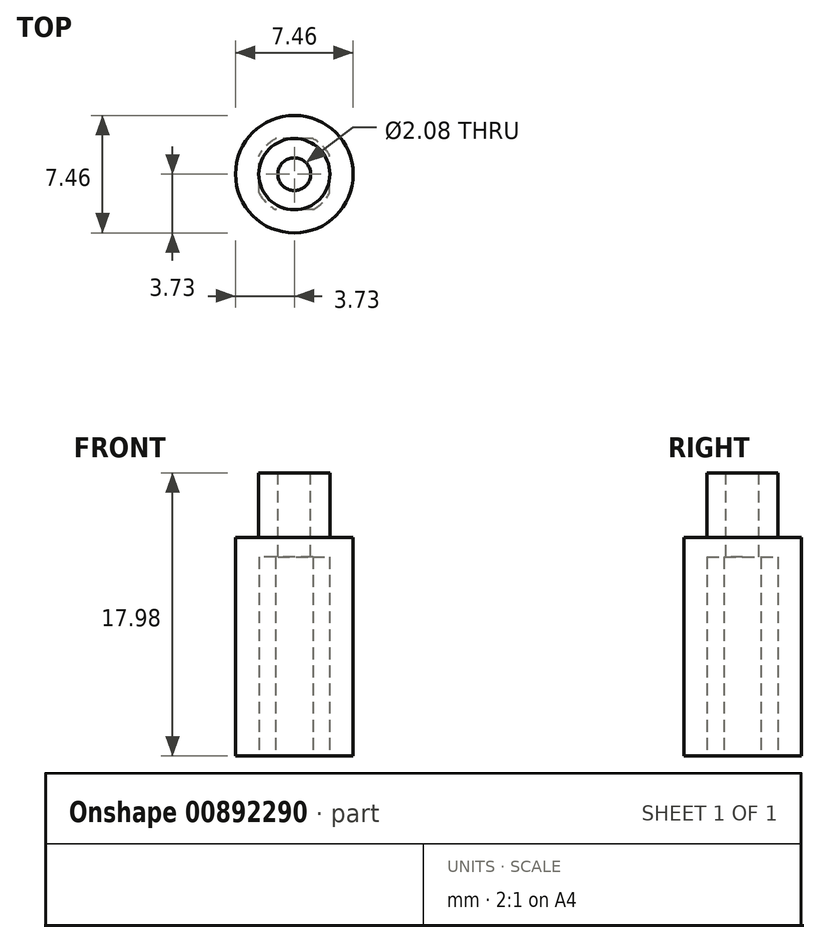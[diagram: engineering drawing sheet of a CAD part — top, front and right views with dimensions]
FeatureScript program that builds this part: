
annotation { "Feature Type Name" : "Feature", "Feature Type Description" : "" }
export const myFeature = defineFeature(function(context is Context, id is Id, definition is map)
    precondition{}
    {
        {
            var Q0;
            Q0=qCreatedBy(makeId("Top.planeOp"),FACE);
            var sketch = newSketch(context, id + "F0", { "sketchPlane" : qUnion([Q0])});
            skCircle(sketch, "E0", {"center": v(0, 0) * mm, "radius": 3.73 * mm});
            skSolve(sketch);
        }
        {
            var Q0;
            Q0 = qSketchRegion(id + "F0", true);
            extrude(context, id + "F1", {"entities" : qUnion([Q0]), "depth" : 13.88 * mm, "offsetDistance" : 25.4 * mm});
        }
        {
            var Q0;
            Q0=makeQuery(id+"F1.opExtrude","CAP_FACE",FACE,{"disambiguationData":[OSD([sQuery(id+"F0.wireOp",EDGE,"E0")])],"isStart":false});
            var sketch = newSketch(context, id + "F2", { "sketchPlane" : qUnion([Q0])});
            skCircle(sketch, "E1", {"center": v(0, 0) * mm, "radius": 2.26 * mm});
            skSolve(sketch);
        }
        {
            var Q0;
            Q0 = qSketchRegion(id + "F2", true);
            extrude(context, id + "F3", {"entities" : qUnion([Q0]), "operationType" : NewBodyOperationType.ADD, "depth" : 4.1 * mm, "offsetDistance" : 25.4 * mm});
        }
        {
            var Q0;
            Q0=makeQuery(id+"F3.opExtrude","CAP_FACE",FACE,{"disambiguationData":[OSD([sQuery(id+"F2.wireOp",EDGE,"E1")])],"isStart":false});
            var sketch = newSketch(context, id + "F4", { "sketchPlane" : qUnion([Q0])});
            skCircle(sketch, "E2", {"center": v(0, 0) * mm, "radius": 1.04 * mm});
            skSolve(sketch);
        }
        {
            var Q0;
            Q0 = qSketchRegion(id + "F4", true);
            extrude(context, id + "F5", {"entities" : qUnion([Q0]), "operationType" : NewBodyOperationType.REMOVE, "oppositeDirection" : true, "depth" : 47.02 * mm, "offsetDistance" : 25.4 * mm});
        }
        {
            var Q0;
            Q0=makeQuery(id+"F1.opExtrude","CAP_FACE",FACE,{"disambiguationData":[OSD([sQuery(id+"F0.wireOp",EDGE,"E0")])],"isStart":true});
            var sketch = newSketch(context, id + "F6", { "sketchPlane" : qUnion([Q0])});
            skCircle(sketch, "E3", {"center": v(0, 0) * mm, "radius": 2.54 * mm});
            skSolve(sketch);
        }
        {
            var Q0;
            Q0 = qSketchRegion(id + "F6", true);
            extrude(context, id + "F7", {"entities" : qUnion([Q0]), "operationType" : NewBodyOperationType.REMOVE, "oppositeDirection" : true, "depth" : 12.65 * mm, "offsetDistance" : 25.4 * mm});
        }
        {
            var Q0;
            Q0=makeQuery(id+"F1.opExtrude","CAP_FACE",FACE,{"disambiguationData":[OSD([sQuery(id+"F0.wireOp",EDGE,"E0")])],"isStart":true});
            var sketch = newSketch(context, id + "F8", { "sketchPlane" : qUnion([Q0])});
            skLineSegment(sketch, "E4.bottom", {"start": v(2.25, 2.25) * mm, "end": v(-2.25, 2.25) * mm});
            skLineSegment(sketch, "E4.top", {"start": v(2.25, -2.25) * mm, "end": v(-2.25, -2.25) * mm});
            skLineSegment(sketch, "E4.left", {"start": v(2.25, 2.25) * mm, "end": v(2.25, -2.25) * mm});
            skLineSegment(sketch, "E4.right", {"start": v(-2.25, 2.25) * mm, "end": v(-2.25, -2.25) * mm});
            skPoint(sketch, "E4.middle", {"position": v(0, 0) * mm});
            skSolve(sketch);
        }
        {
            var Q0;
            {var subQ0=sQuery(id+"F8.wireOp",EDGE,"E4.bottom");var subQ1=makeQuery(id+"F7.boolean.opBoolean","COPY",EDGE,{"derivedFrom":makeQuery(id+"F7.opExtrude","CAP_EDGE",EDGE,{"disambiguationData":[OSD([sQuery(id+"F6.wireOp",EDGE,"E3")])],"isStart":true})});var subQ2=makeQuery(id+"F8.imprint","INTERSECT",VERTEX,{"disambiguationData":[OD(0.0)],"derivedFrom":[subQ1,subQ0]});Q0=makeQuery(id+"F8.imprint","IMPRINT",FACE,{"disambiguationData":[TD([[makeQuery(id+"F8.imprint","IMPRINT",EDGE,{"disambiguationData":[TD([[subQ2,-1.0]])],"derivedFrom":subQ0}),-1.0]])]});}
            var Q1;
            {var subQ0=sQuery(id+"F8.wireOp",EDGE,"E4.right");var subQ1=makeQuery(id+"F7.boolean.opBoolean","COPY",EDGE,{"derivedFrom":makeQuery(id+"F7.opExtrude","CAP_EDGE",EDGE,{"disambiguationData":[OSD([sQuery(id+"F6.wireOp",EDGE,"E3")])],"isStart":true})});var subQ2=makeQuery(id+"F8.imprint","INTERSECT",VERTEX,{"disambiguationData":[OD(0.0)],"derivedFrom":[subQ1,subQ0]});Q1=makeQuery(id+"F8.imprint","IMPRINT",FACE,{"disambiguationData":[TD([[makeQuery(id+"F8.imprint","IMPRINT",EDGE,{"disambiguationData":[TD([[subQ2,-1.0]])],"derivedFrom":subQ0}),-1.0]])]});}
            var Q2;
            {var subQ0=sQuery(id+"F8.wireOp",EDGE,"E4.top");var subQ1=makeQuery(id+"F7.boolean.opBoolean","COPY",EDGE,{"derivedFrom":makeQuery(id+"F7.opExtrude","CAP_EDGE",EDGE,{"disambiguationData":[OSD([sQuery(id+"F6.wireOp",EDGE,"E3")])],"isStart":true})});var subQ2=makeQuery(id+"F8.imprint","INTERSECT",VERTEX,{"disambiguationData":[OD(0.0)],"derivedFrom":[subQ1,subQ0]});Q2=makeQuery(id+"F8.imprint","IMPRINT",FACE,{"disambiguationData":[TD([[makeQuery(id+"F8.imprint","IMPRINT",EDGE,{"disambiguationData":[TD([[subQ2,-1.0]])],"derivedFrom":subQ0}),1.0]])]});}
            var Q3;
            {var subQ0=sQuery(id+"F8.wireOp",EDGE,"E4.left");var subQ1=makeQuery(id+"F7.boolean.opBoolean","COPY",EDGE,{"derivedFrom":makeQuery(id+"F7.opExtrude","CAP_EDGE",EDGE,{"disambiguationData":[OSD([sQuery(id+"F6.wireOp",EDGE,"E3")])],"isStart":true})});var subQ2=makeQuery(id+"F8.imprint","INTERSECT",VERTEX,{"disambiguationData":[OD(0.0)],"derivedFrom":[subQ1,subQ0]});Q3=makeQuery(id+"F8.imprint","IMPRINT",FACE,{"disambiguationData":[TD([[makeQuery(id+"F8.imprint","IMPRINT",EDGE,{"disambiguationData":[TD([[subQ2,-1.0]])],"derivedFrom":subQ0}),1.0]])]});}
            extrude(context, id + "F9", {"entities" : qUnion([Q0, Q1, Q2, Q3]), "operationType" : NewBodyOperationType.ADD, "oppositeDirection" : true, "depth" : 13.54 * mm, "offsetDistance" : 25.4 * mm});
        }
    });
